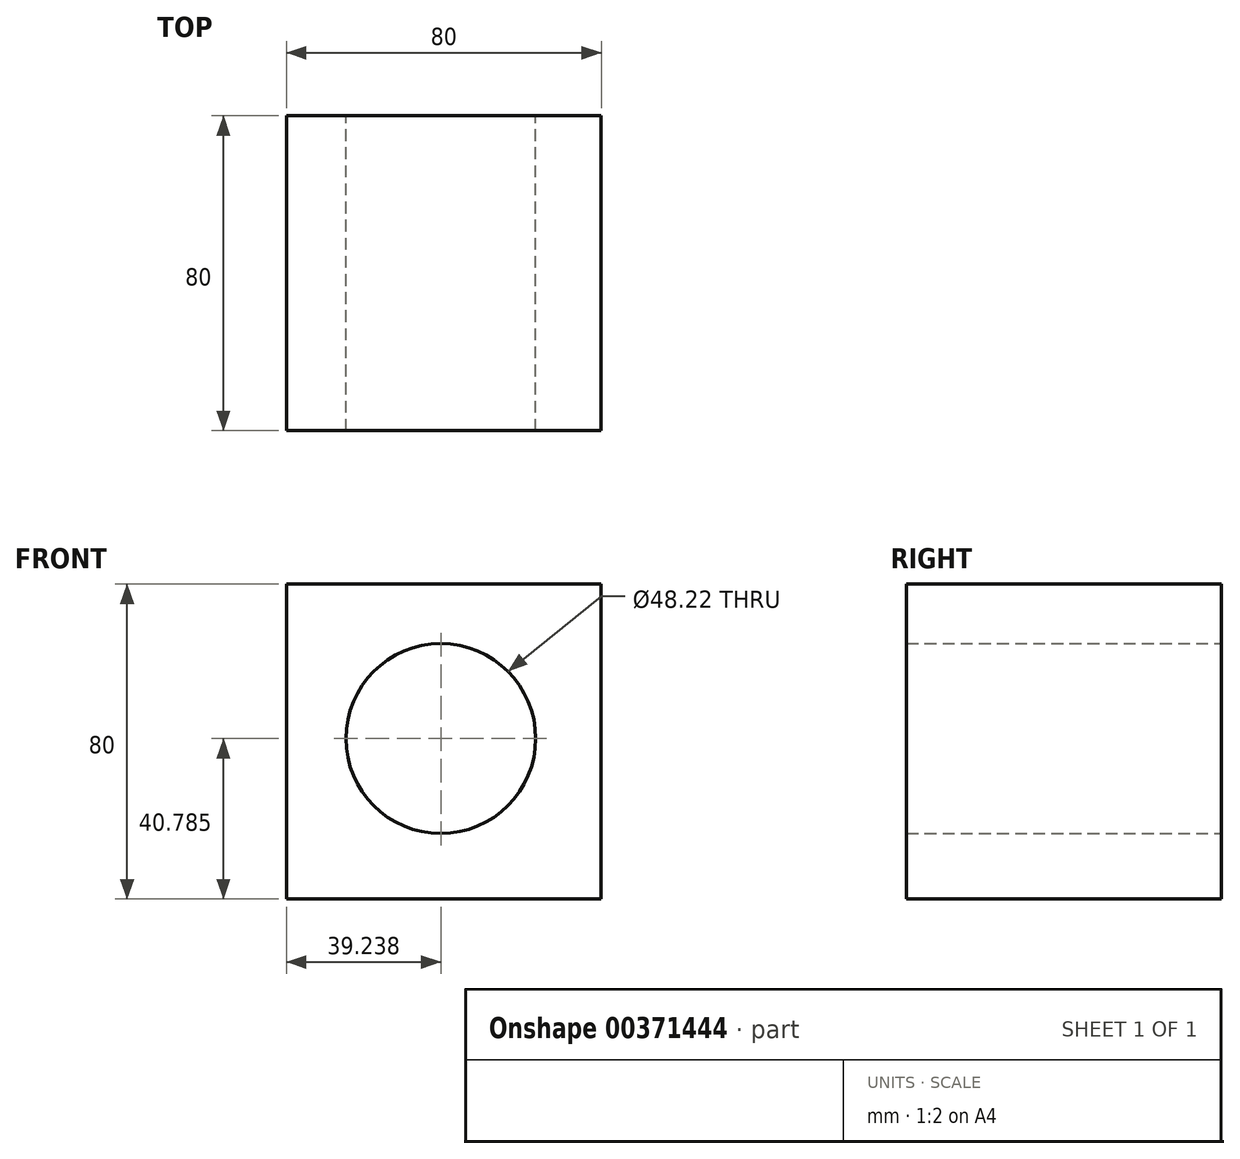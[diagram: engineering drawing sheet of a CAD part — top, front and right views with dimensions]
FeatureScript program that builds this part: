
annotation { "Feature Type Name" : "Feature", "Feature Type Description" : "" }
export const myFeature = defineFeature(function(context is Context, id is Id, definition is map)
    precondition{}
    {
        {
            var Q0;
            Q0=qCreatedBy(makeId("Top.planeOp"),FACE);
            var sketch = newSketch(context, id + "F0", { "sketchPlane" : qUnion([Q0])});
            skLineSegment(sketch, "E0.bottom", {"start": v(-77.26, 52.04) * mm, "end": v(2.74, 52.04) * mm});
            skLineSegment(sketch, "E0.top", {"start": v(-77.26, -27.96) * mm, "end": v(2.74, -27.96) * mm});
            skLineSegment(sketch, "E0.left", {"start": v(-77.26, 52.04) * mm, "end": v(-77.26, -27.96) * mm});
            skLineSegment(sketch, "E0.right", {"start": v(2.74, 52.04) * mm, "end": v(2.74, -27.96) * mm});
            skSolve(sketch);
        }
        {
            var Q0;
            Q0=makeQuery(id+"F0.imprint","IMPRINT",FACE,{"disambiguationData":[TD([[makeQuery(id+"F0.imprint","IMPRINT",EDGE,{"derivedFrom":sQuery(id+"F0.wireOp",EDGE,"E0.bottom")}),-1.0]])]});
            extrude(context, id + "F1", {"entities" : qUnion([Q0]), "depth" : 80 * mm});
        }
        {
            var Q0;
            Q0=makeQuery(id+"F1.opExtrude","SWEPT_FACE",FACE,{"disambiguationData":[OSD([sQuery(id+"F0.wireOp",EDGE,"E0.bottom")])]});
            var sketch = newSketch(context, id + "F2", { "sketchPlane" : qUnion([Q0])});
            skCircle(sketch, "E1", {"center": v(38.02, 40.78) * mm, "radius": 24.11 * mm});
            skSolve(sketch);
        }
        {
            var Q0;
            Q0 = qSketchRegion(id + "F2", true);
            extrude(context, id + "F3", {"entities" : qUnion([Q0]), "operationType" : NewBodyOperationType.REMOVE, "endBound" : BoundingType.THROUGH_ALL, "oppositeDirection" : true, "depth" : 25 * mm});
        }
    });
